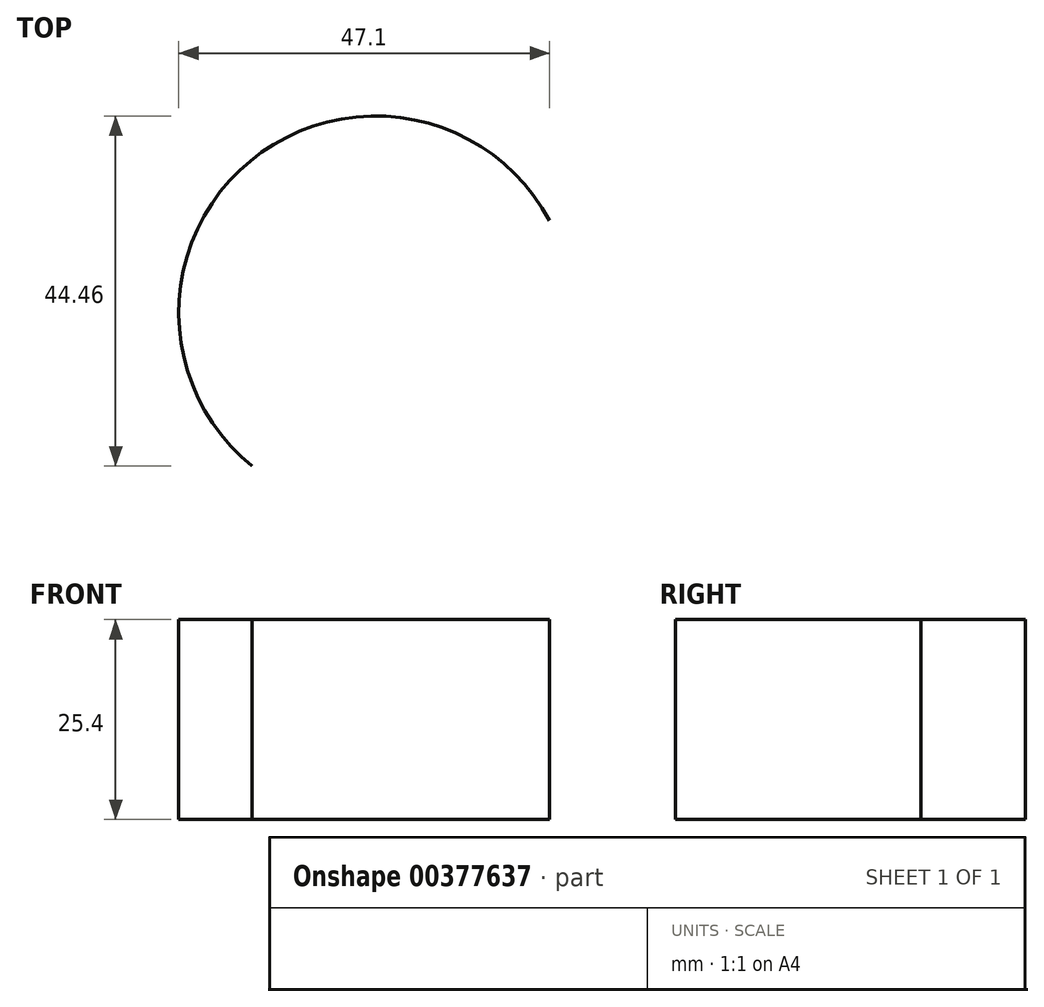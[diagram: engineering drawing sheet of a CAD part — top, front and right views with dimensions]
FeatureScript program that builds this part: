
annotation { "Feature Type Name" : "Feature", "Feature Type Description" : "" }
export const myFeature = defineFeature(function(context is Context, id is Id, definition is map)
    precondition{}
    {
        {
            var Q0;
            Q0=qCreatedBy(makeId("Top.planeOp"),FACE);
            var sketch = newSketch(context, id + "F0", { "sketchPlane" : qUnion([Q0])});
            skArc(sketch, "E0", {"start": v(-10.75, 52.49) * mm, "mid": v(-48.76, 60.08) * mm, "end": v(-48.53, 21.33) * mm});
            skArc(sketch, "E1", {"start": v(43.47, 10.93) * mm, "mid": v(48.9, 44.43) * mm, "end": v(15.93, 52.47) * mm});
            skSolve(sketch);
        }
        {
            var Q0;
            Q0=sQuery(id+"F0.wireOp",EDGE,"E0");
            extrude(context, id + "F1", {"bodyType" : ToolBodyType.SURFACE, "surfaceEntities" : qUnion([Q0]), "depth" : 25.4 * mm});
        }
    });
